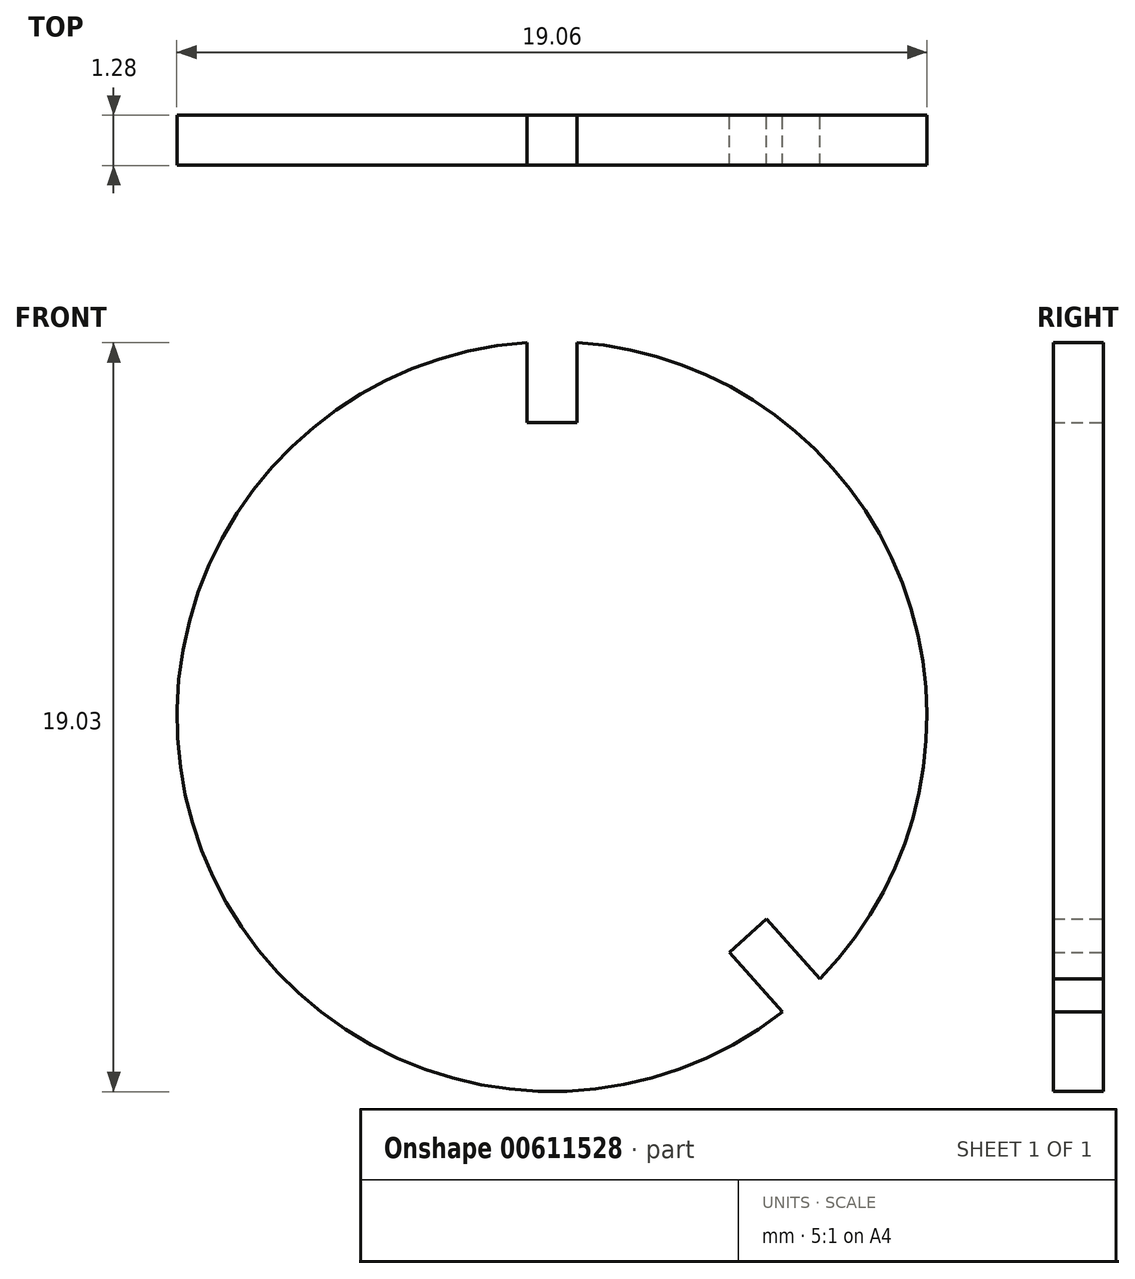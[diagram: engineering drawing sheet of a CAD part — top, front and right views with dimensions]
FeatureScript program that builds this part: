
annotation { "Feature Type Name" : "Feature", "Feature Type Description" : "" }
export const myFeature = defineFeature(function(context is Context, id is Id, definition is map)
    precondition{}
    {
        {
            var Q0;
            Q0=qCreatedBy(makeId("Front.planeOp"),FACE);
            var sketch = newSketch(context, id + "F0", { "sketchPlane" : qUnion([Q0])});
            skArc(sketch, "E0", {"start": v(6.8, -6.66) * mm, "mid": v(8.9, 3.4) * mm, "end": v(0.64, 9.5) * mm});
            skLineSegment(sketch, "E1.top", {"start": v(-0.64, 7.47) * mm, "end": v(0.64, 7.47) * mm});
            skLineSegment(sketch, "E1.left", {"start": v(-0.64, 9.5) * mm, "end": v(-0.64, 7.47) * mm});
            skLineSegment(sketch, "E1.right", {"start": v(0.64, 9.5) * mm, "end": v(0.64, 7.47) * mm});
            skLineSegment(sketch, "E2.1.0", {"start": v(5.86, -7.5) * mm, "end": v(4.5, -6) * mm});
            skLineSegment(sketch, "E2.1.1", {"start": v(5.45, -5.15) * mm, "end": v(4.5, -6) * mm});
            skLineSegment(sketch, "E2.1.2", {"start": v(6.8, -6.66) * mm, "end": v(5.45, -5.15) * mm});
            skLineSegment(sketch, "E2.anchor1", {"start": v(0, 0) * mm, "end": v(0.63, 7.47) * mm, "construction": true});
            skLineSegment(sketch, "E2.anchor2", {"start": v(0, 0) * mm, "end": v(4.5, -6) * mm, "construction": true});
            skArc(sketch, "E3.trimOffspring", {"start": v(-0.63, 9.5) * mm, "mid": v(-8.9, -3.4) * mm, "end": v(5.86, -7.5) * mm});
            skSolve(sketch);
        }
        {
            var Q0;
            Q0 = qSketchRegion(id + "F0", true);
            extrude(context, id + "F1", {"entities" : qUnion([Q0]), "endBound" : BoundingType.SYMMETRIC, "depth" : 1.27 * mm, "offsetDistance" : 25.4 * mm});
        }
    });
